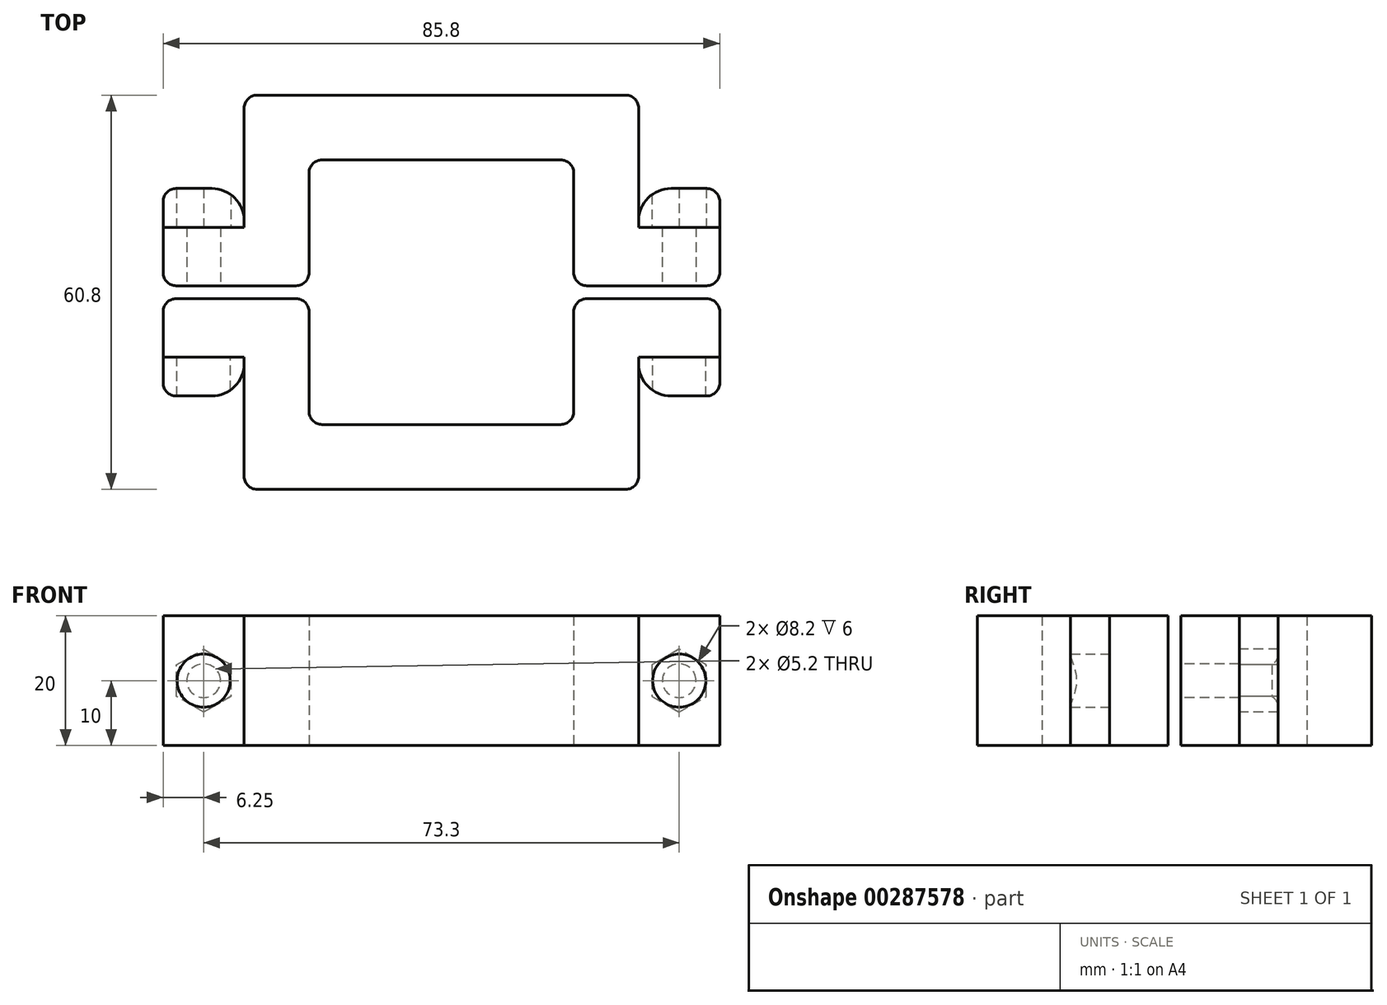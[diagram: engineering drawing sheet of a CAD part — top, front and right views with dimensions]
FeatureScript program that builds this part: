
annotation { "Feature Type Name" : "Feature", "Feature Type Description" : "" }
export const myFeature = defineFeature(function(context is Context, id is Id, definition is map)
    precondition{}
    {
        {
            var Q0;
            Q0=qCreatedBy(makeId("Top.planeOp"),FACE);
            var sketch = newSketch(context, id + "F0", { "sketchPlane" : qUnion([Q0])});
            skLineSegment(sketch, "E0.bottom", {"start": v(20.4, -20.4) * mm, "end": v(-20.4, -20.4) * mm});
            skLineSegment(sketch, "E0.top", {"start": v(20.4, 20.4) * mm, "end": v(-20.4, 20.4) * mm});
            skLineSegment(sketch, "E0.left", {"start": v(20.4, -20.4) * mm, "end": v(20.4, 20.4) * mm});
            skLineSegment(sketch, "E0.right", {"start": v(-20.4, -20.4) * mm, "end": v(-20.4, 20.4) * mm});
            skPoint(sketch, "E0.middle", {"position": v(0, 0) * mm});
            skLineSegment(sketch, "E1.bottom", {"start": v(30.4, -30.4) * mm, "end": v(-30.4, -30.4) * mm});
            skLineSegment(sketch, "E1.top", {"start": v(30.4, 30.4) * mm, "end": v(-30.4, 30.4) * mm});
            skLineSegment(sketch, "E1.left", {"start": v(30.4, -30.4) * mm, "end": v(30.4, 30.4) * mm});
            skLineSegment(sketch, "E1.right", {"start": v(-30.4, -30.4) * mm, "end": v(-30.4, 30.4) * mm});
            skLineSegment(sketch, "E2.bottom", {"start": v(42.9, -10) * mm, "end": v(17.9, -10) * mm});
            skLineSegment(sketch, "E2.top", {"start": v(42.9, 10) * mm, "end": v(17.9, 10) * mm});
            skLineSegment(sketch, "E2.left", {"start": v(42.9, -10) * mm, "end": v(42.9, 10) * mm});
            skLineSegment(sketch, "E2.right", {"start": v(17.9, -10) * mm, "end": v(17.9, 10) * mm});
            skPoint(sketch, "E2.middle", {"position": v(30.4, 0) * mm});
            skLineSegment(sketch, "E3.MirrorCS", {"start": v(-42.9, -10) * mm, "end": v(-17.9, -10) * mm});
            skLineSegment(sketch, "E4.MirrorCS", {"start": v(-42.9, 10) * mm, "end": v(-17.9, 10) * mm});
            skLineSegment(sketch, "E5.MirrorCS", {"start": v(-17.9, -10) * mm, "end": v(-17.9, 10) * mm});
            skLineSegment(sketch, "E6.MirrorCS", {"start": v(-42.9, -10) * mm, "end": v(-42.9, 10) * mm});
            skLineSegment(sketch, "E7.bottom", {"start": v(42.9, 1) * mm, "end": v(-42.9, 1) * mm});
            skLineSegment(sketch, "E7.top", {"start": v(42.9, -1) * mm, "end": v(-42.9, -1) * mm});
            skLineSegment(sketch, "E7.left", {"start": v(42.9, 1) * mm, "end": v(42.9, -1) * mm});
            skLineSegment(sketch, "E7.right", {"start": v(-42.9, 1) * mm, "end": v(-42.9, -1) * mm});
            skSolve(sketch);
        }
        {
            var Q0;
            {var subQ2=sQuery(id+"F0.wireOp",EDGE,"E0.top");Q0=makeQuery(id+"F0.imprint","IMPRINT",FACE,{"disambiguationData":[TD([[makeQuery(id+"F0.imprint","IMPRINT",EDGE,{"derivedFrom":subQ2}),-1.0]])]});}
            var Q1;
            {var subQ0=sQuery(id+"F0.wireOp",EDGE,"E7.bottom");var subQ1=sQuery(id+"F0.wireOp",EDGE,"E0.right");var subQ2=makeQuery(id+"F0.imprint","INTERSECT",VERTEX,{"derivedFrom":[subQ1,subQ0]});Q1=makeQuery(id+"F0.imprint","IMPRINT",FACE,{"disambiguationData":[TD([[makeQuery(id+"F0.imprint","IMPRINT",EDGE,{"disambiguationData":[TD([[subQ2,-1.0]])],"derivedFrom":subQ1}),1.0]])]});}
            var Q2;
            {var subQ0=sQuery(id+"F0.wireOp",EDGE,"E4.MirrorCS");var subQ1=sQuery(id+"F0.wireOp",EDGE,"E1.right");var subQ2=makeQuery(id+"F0.imprint","INTERSECT",VERTEX,{"derivedFrom":[subQ1,subQ0]});Q2=makeQuery(id+"F0.imprint","IMPRINT",FACE,{"disambiguationData":[TD([[makeQuery(id+"F0.imprint","IMPRINT",EDGE,{"disambiguationData":[TD([[subQ2,1.0]])],"derivedFrom":subQ1}),1.0]])]});}
            var Q3;
            {var subQ0=sQuery(id+"F0.wireOp",EDGE,"E3.MirrorCS");var subQ1=sQuery(id+"F0.wireOp",EDGE,"E1.right");var subQ2=makeQuery(id+"F0.imprint","INTERSECT",VERTEX,{"derivedFrom":[subQ1,subQ0]});Q3=makeQuery(id+"F0.imprint","IMPRINT",FACE,{"disambiguationData":[TD([[makeQuery(id+"F0.imprint","IMPRINT",EDGE,{"disambiguationData":[TD([[subQ2,-1.0]])],"derivedFrom":subQ1}),1.0]])]});}
            var Q4;
            {var subQ0=sQuery(id+"F0.wireOp",EDGE,"E3.MirrorCS");var subQ1=sQuery(id+"F0.wireOp",EDGE,"E0.right");var subQ2=makeQuery(id+"F0.imprint","INTERSECT",VERTEX,{"derivedFrom":[subQ1,subQ0]});Q4=makeQuery(id+"F0.imprint","IMPRINT",FACE,{"disambiguationData":[TD([[makeQuery(id+"F0.imprint","IMPRINT",EDGE,{"disambiguationData":[TD([[subQ2,-1.0]])],"derivedFrom":subQ1}),1.0]])]});}
            var Q5;
            {var subQ2=sQuery(id+"F0.wireOp",EDGE,"E0.bottom");Q5=makeQuery(id+"F0.imprint","IMPRINT",FACE,{"disambiguationData":[TD([[makeQuery(id+"F0.imprint","IMPRINT",EDGE,{"derivedFrom":subQ2}),1.0]])]});}
            var Q6;
            {var subQ0=sQuery(id+"F0.wireOp",EDGE,"E2.bottom");var subQ1=sQuery(id+"F0.wireOp",EDGE,"E1.left");var subQ2=makeQuery(id+"F0.imprint","INTERSECT",VERTEX,{"derivedFrom":[subQ1,subQ0]});Q6=makeQuery(id+"F0.imprint","IMPRINT",FACE,{"disambiguationData":[TD([[makeQuery(id+"F0.imprint","IMPRINT",EDGE,{"disambiguationData":[TD([[subQ2,-1.0]])],"derivedFrom":subQ1}),-1.0]])]});}
            var Q7;
            {var subQ0=sQuery(id+"F0.wireOp",EDGE,"E2.bottom");var subQ1=sQuery(id+"F0.wireOp",EDGE,"E0.left");var subQ2=makeQuery(id+"F0.imprint","INTERSECT",VERTEX,{"derivedFrom":[subQ1,subQ0]});Q7=makeQuery(id+"F0.imprint","IMPRINT",FACE,{"disambiguationData":[TD([[makeQuery(id+"F0.imprint","IMPRINT",EDGE,{"disambiguationData":[TD([[subQ2,-1.0]])],"derivedFrom":subQ1}),-1.0]])]});}
            var Q8;
            {var subQ0=sQuery(id+"F0.wireOp",EDGE,"E2.top");var subQ1=sQuery(id+"F0.wireOp",EDGE,"E1.left");var subQ2=makeQuery(id+"F0.imprint","INTERSECT",VERTEX,{"derivedFrom":[subQ1,subQ0]});Q8=makeQuery(id+"F0.imprint","IMPRINT",FACE,{"disambiguationData":[TD([[makeQuery(id+"F0.imprint","IMPRINT",EDGE,{"disambiguationData":[TD([[subQ2,1.0]])],"derivedFrom":subQ1}),-1.0]])]});}
            var Q9;
            {var subQ0=sQuery(id+"F0.wireOp",EDGE,"E2.top");var subQ1=sQuery(id+"F0.wireOp",EDGE,"E0.left");var subQ2=makeQuery(id+"F0.imprint","INTERSECT",VERTEX,{"derivedFrom":[subQ1,subQ0]});Q9=makeQuery(id+"F0.imprint","IMPRINT",FACE,{"disambiguationData":[TD([[makeQuery(id+"F0.imprint","IMPRINT",EDGE,{"disambiguationData":[TD([[subQ2,1.0]])],"derivedFrom":subQ1}),-1.0]])]});}
            extrude(context, id + "F1", {"entities" : qUnion([Q0, Q1, Q2, Q3, Q4, Q5, Q6, Q7, Q8, Q9]), "depth" : 20 * mm, "offsetDistance" : 25 * mm});
        }
        {
            var Q0;
            Q0=makeQuery(id+"F1.opExtrude","SWEPT_FACE",FACE,{"disambiguationData":[OSD([sQuery(id+"F0.wireOp",EDGE,"E2.bottom")])]});
            var sketch = newSketch(context, id + "F2", { "sketchPlane" : qUnion([Q0])});
            skCircle(sketch, "E8", {"center": v(36.65, 10) * mm, "radius": 2.6 * mm});
            skPoint(sketch, "E8.centerSnap0", {"position": v(36.65, 20) * mm});
            skPoint(sketch, "E8.centerSnap1", {"position": v(42.9, 10) * mm});
            skCircle(sketch, "E9", {"center": v(36.65, 10) * mm, "radius": 4.1 * mm});
            skSolve(sketch);
        }
        {
            var Q0;
            Q0=makeQuery(id+"F2.imprint","IMPRINT",FACE,{"disambiguationData":[TD([[makeQuery(id+"F2.imprint","IMPRINT",EDGE,{"derivedFrom":sQuery(id+"F2.wireOp",EDGE,"E8")}),1.0]])]});
            var Q1;
            Q1=makeQuery(id+"F1.opExtrude","SWEPT_FACE",FACE,{"disambiguationData":[OSD([sQuery(id+"F0.wireOp",EDGE,"E2.top")])]});
            extrude(context, id + "F3", {"entities" : qUnion([Q0]), "endBound" : BoundingType.UP_TO_SURFACE, "oppositeDirection" : true, "depth" : 25 * mm, "endBoundEntityFace" : qUnion([Q1]), "offsetDistance" : 25 * mm});
        }
        {
            var Q0;
            Q0=makeQuery(id+"F2.imprint","IMPRINT",FACE,{"disambiguationData":[TD([[makeQuery(id+"F2.imprint","IMPRINT",EDGE,{"derivedFrom":sQuery(id+"F2.wireOp",EDGE,"E9")}),-1.0]])]});
            extrude(context, id + "F4", {"entities" : qUnion([Q0]), "depth" : 6 * mm, "offsetDistance" : 25 * mm});
        }
        {
            var Q0;
            Q0=makeQuery(id+"F1.opExtrude","SWEPT_FACE",FACE,{"disambiguationData":[OSD([sQuery(id+"F0.wireOp",EDGE,"E2.top")])]});
            var sketch = newSketch(context, id + "F5", { "sketchPlane" : qUnion([Q0])});
            skCircle(sketch, "E10.cCircle", {"center": v(-36.65, 10) * mm, "radius": 4.2 * mm, "construction": true});
            skPoint(sketch, "E10.cCircle.centerSnap0", {"position": v(-42.9, 10) * mm});
            skPoint(sketch, "E10.cCircle.centerSnap1", {"position": v(-36.65, 20) * mm});
            skLineSegment(sketch, "E10.0", {"start": v(-32.45, 7.58) * mm, "end": v(-36.65, 5.15) * mm});
            skLineSegment(sketch, "E10.1", {"start": v(-36.65, 5.15) * mm, "end": v(-40.85, 7.58) * mm});
            skLineSegment(sketch, "E10.2", {"start": v(-40.85, 7.58) * mm, "end": v(-40.85, 12.42) * mm});
            skLineSegment(sketch, "E10.3", {"start": v(-40.85, 12.42) * mm, "end": v(-36.65, 14.85) * mm});
            skLineSegment(sketch, "E10.4", {"start": v(-36.65, 14.85) * mm, "end": v(-32.45, 12.42) * mm});
            skLineSegment(sketch, "E10.5", {"start": v(-32.45, 12.42) * mm, "end": v(-32.45, 7.58) * mm});
            skPoint(sketch, "E10.0.midPoint", {"position": v(-34.55, 6.36) * mm});
            skSolve(sketch);
        }
        {
            var Q0;
            Q0=makeQuery(id+"F5.imprint","IMPRINT",FACE,{"disambiguationData":[TD([[makeQuery(id+"F5.imprint","IMPRINT",EDGE,{"derivedFrom":sQuery(id+"F5.wireOp",EDGE,"E10.0")}),1.0]])]});
            extrude(context, id + "F6", {"entities" : qUnion([Q0]), "depth" : 6 * mm, "offsetDistance" : 25 * mm});
        }
        {
            var Q0;
            Q0=makeQuery(id+"F4.opExtrude","SWEPT_BODY",BODY,{"disambiguationData":[OSD([sQuery(id+"F0.wireOp",EDGE,"E1.left"),sQuery(id+"F0.wireOp",EDGE,"E2.bottom"),sQuery(id+"F0.wireOp",EDGE,"E2.left"),sQuery(id+"F2.wireOp",EDGE,"E9")])]});
            var Q1;
            Q1=makeQuery(id+"F3.opExtrude","SWEPT_BODY",BODY,{"disambiguationData":[OSD([sQuery(id+"F2.wireOp",EDGE,"E8")])]});
            var Q2;
            Q2=makeQuery(id+"F6.opExtrude","SWEPT_BODY",BODY,{"disambiguationData":[OSD([sQuery(id+"F0.wireOp",EDGE,"E1.left"),sQuery(id+"F0.wireOp",EDGE,"E2.top"),sQuery(id+"F0.wireOp",EDGE,"E2.left"),sQuery(id+"F5.wireOp",EDGE,"E10.0"),sQuery(id+"F5.wireOp",EDGE,"E10.1"),sQuery(id+"F5.wireOp",EDGE,"E10.2"),sQuery(id+"F5.wireOp",EDGE,"E10.3"),sQuery(id+"F5.wireOp",EDGE,"E10.4"),sQuery(id+"F5.wireOp",EDGE,"E10.5")])]});
            var Q3;
            Q3=qCreatedBy(makeId("Right.planeOp"),FACE);
            mirror(context, id + "F7", {"entities" : qUnion([Q0, Q1, Q2]), "mirrorPlane" : qUnion([Q3])});
        }
        {
            var Q0;
            Q0=makeQuery(id+"F7.opPattern","COPY",BODY,{"derivedFrom":makeQuery(id+"F3.opExtrude","SWEPT_BODY",BODY,{"disambiguationData":[OSD([sQuery(id+"F2.wireOp",EDGE,"E8")])]}),"instanceName":"1"});
            var Q1;
            Q1=makeQuery(id+"F3.opExtrude","SWEPT_BODY",BODY,{"disambiguationData":[OSD([sQuery(id+"F2.wireOp",EDGE,"E8")])]});
            var Q2;
            Q2=makeQuery(id+"F4.opExtrude","SWEPT_BODY",BODY,{"disambiguationData":[OSD([sQuery(id+"F0.wireOp",EDGE,"E1.left"),sQuery(id+"F0.wireOp",EDGE,"E2.bottom"),sQuery(id+"F0.wireOp",EDGE,"E2.left"),sQuery(id+"F2.wireOp",EDGE,"E9")])]});
            var Q3;
            Q3=makeQuery(id+"F1.opExtrude","SWEPT_BODY",BODY,{"disambiguationData":[OSD([sQuery(id+"F0.wireOp",EDGE,"E0.top"),sQuery(id+"F0.wireOp",EDGE,"E0.left"),sQuery(id+"F0.wireOp",EDGE,"E0.right"),sQuery(id+"F0.wireOp",EDGE,"E1.top"),sQuery(id+"F0.wireOp",EDGE,"E1.left"),sQuery(id+"F0.wireOp",EDGE,"E1.right"),sQuery(id+"F0.wireOp",EDGE,"E2.top"),sQuery(id+"F0.wireOp",EDGE,"E2.left"),sQuery(id+"F0.wireOp",EDGE,"E4.MirrorCS"),sQuery(id+"F0.wireOp",EDGE,"E6.MirrorCS"),sQuery(id+"F0.wireOp",EDGE,"E7.bottom")])]});
            booleanBodies(context, id + "F8", {"operationType" : BooleanOperationType.SUBTRACTION, "tools" : qUnion([Q0, Q1]), "targets" : qUnion([Q2, Q3])});
        }
        {
            var Q0;
            Q0=makeQuery(id+"F1.opExtrude","SWEPT_EDGE",EDGE,{"disambiguationData":[OSD([sQuery(id+"F0.wireOp",EDGE,"E0.top"),sQuery(id+"F0.wireOp",EDGE,"E0.right")])]});
            var Q1;
            Q1=makeQuery(id+"F1.opExtrude","SWEPT_EDGE",EDGE,{"disambiguationData":[OSD([sQuery(id+"F0.wireOp",EDGE,"E0.top"),sQuery(id+"F0.wireOp",EDGE,"E0.left")])]});
            var Q2;
            Q2=makeQuery(id+"F1.opExtrude","SWEPT_EDGE",EDGE,{"disambiguationData":[OSD([sQuery(id+"F0.wireOp",EDGE,"E0.bottom"),sQuery(id+"F0.wireOp",EDGE,"E0.left")])]});
            var Q3;
            Q3=makeQuery(id+"F1.opExtrude","SWEPT_EDGE",EDGE,{"disambiguationData":[OSD([sQuery(id+"F0.wireOp",EDGE,"E0.bottom"),sQuery(id+"F0.wireOp",EDGE,"E0.right")])]});
            fillet(context, id + "F9", {"entities" : qUnion([Q0, Q1, Q2, Q3]), "tangentPropagation" : true, "radius" : 2 * mm, "defaultsChanged" : true, "vertexSettings" : [], "allowEdgeOverflow" : false});
        }
        {
            var Q0;
            Q0=makeQuery(id+"F1.opExtrude","SWEPT_EDGE",EDGE,{"disambiguationData":[OSD([sQuery(id+"F0.wireOp",EDGE,"E0.right"),sQuery(id+"F0.wireOp",EDGE,"E7.bottom")])]});
            var Q1;
            Q1=makeQuery(id+"F1.opExtrude","SWEPT_EDGE",EDGE,{"disambiguationData":[OSD([sQuery(id+"F0.wireOp",EDGE,"E0.right"),sQuery(id+"F0.wireOp",EDGE,"E7.top")])]});
            var Q2;
            Q2=makeQuery(id+"F1.opExtrude","SWEPT_EDGE",EDGE,{"disambiguationData":[OSD([sQuery(id+"F0.wireOp",EDGE,"E0.left"),sQuery(id+"F0.wireOp",EDGE,"E7.top")])]});
            var Q3;
            Q3=makeQuery(id+"F1.opExtrude","SWEPT_EDGE",EDGE,{"disambiguationData":[OSD([sQuery(id+"F0.wireOp",EDGE,"E0.left"),sQuery(id+"F0.wireOp",EDGE,"E7.bottom")])]});
            var Q4;
            Q4=makeQuery(id+"F1.opExtrude","SWEPT_EDGE",EDGE,{"disambiguationData":[OSD([sQuery(id+"F0.wireOp",EDGE,"E2.left"),sQuery(id+"F0.wireOp",EDGE,"E7.top")])]});
            var Q5;
            Q5=makeQuery(id+"F6.opExtrude","CAP_EDGE",EDGE,{"disambiguationData":[OSD([sQuery(id+"F0.wireOp",EDGE,"E2.top"),sQuery(id+"F0.wireOp",EDGE,"E2.left")])],"isStart":false});
            var Q6;
            Q6=makeQuery(id+"F4.opExtrude","CAP_EDGE",EDGE,{"disambiguationData":[OSD([sQuery(id+"F0.wireOp",EDGE,"E2.bottom"),sQuery(id+"F0.wireOp",EDGE,"E2.left")])],"isStart":false});
            var Q7;
            Q7=makeQuery(id+"F1.opExtrude","SWEPT_EDGE",EDGE,{"disambiguationData":[OSD([sQuery(id+"F0.wireOp",EDGE,"E2.left"),sQuery(id+"F0.wireOp",EDGE,"E7.bottom")])]});
            var Q8;
            Q8=makeQuery(id+"F7.opPattern","COPY",EDGE,{"derivedFrom":makeQuery(id+"F4.opExtrude","CAP_EDGE",EDGE,{"disambiguationData":[OSD([sQuery(id+"F0.wireOp",EDGE,"E2.bottom"),sQuery(id+"F0.wireOp",EDGE,"E2.left")])],"isStart":false}),"instanceName":"1"});
            var Q9;
            Q9=makeQuery(id+"F1.opExtrude","SWEPT_EDGE",EDGE,{"disambiguationData":[OSD([sQuery(id+"F0.wireOp",EDGE,"E6.MirrorCS"),sQuery(id+"F0.wireOp",EDGE,"E7.top")])]});
            var Q10;
            Q10=makeQuery(id+"F1.opExtrude","SWEPT_EDGE",EDGE,{"disambiguationData":[OSD([sQuery(id+"F0.wireOp",EDGE,"E6.MirrorCS"),sQuery(id+"F0.wireOp",EDGE,"E7.bottom")])]});
            var Q11;
            Q11=makeQuery(id+"F7.opPattern","COPY",EDGE,{"derivedFrom":makeQuery(id+"F6.opExtrude","CAP_EDGE",EDGE,{"disambiguationData":[OSD([sQuery(id+"F0.wireOp",EDGE,"E2.top"),sQuery(id+"F0.wireOp",EDGE,"E2.left")])],"isStart":false}),"instanceName":"1"});
            var Q12;
            Q12=makeQuery(id+"F1.opExtrude","SWEPT_EDGE",EDGE,{"disambiguationData":[OSD([sQuery(id+"F0.wireOp",EDGE,"E1.bottom"),sQuery(id+"F0.wireOp",EDGE,"E1.left")])]});
            var Q13;
            Q13=makeQuery(id+"F1.opExtrude","SWEPT_EDGE",EDGE,{"disambiguationData":[OSD([sQuery(id+"F0.wireOp",EDGE,"E1.bottom"),sQuery(id+"F0.wireOp",EDGE,"E1.right")])]});
            var Q14;
            Q14=makeQuery(id+"F1.opExtrude","SWEPT_EDGE",EDGE,{"disambiguationData":[OSD([sQuery(id+"F0.wireOp",EDGE,"E1.top"),sQuery(id+"F0.wireOp",EDGE,"E1.left")])]});
            var Q15;
            Q15=makeQuery(id+"F1.opExtrude","SWEPT_EDGE",EDGE,{"disambiguationData":[OSD([sQuery(id+"F0.wireOp",EDGE,"E1.top"),sQuery(id+"F0.wireOp",EDGE,"E1.right")])]});
            fillet(context, id + "F10", {"entities" : qUnion([Q0, Q1, Q2, Q3, Q4, Q5, Q6, Q7, Q8, Q9, Q10, Q11, Q12, Q13, Q14, Q15]), "tangentPropagation" : true, "radius" : 2 * mm, "defaultsChanged" : false, "vertexSettings" : [], "allowEdgeOverflow" : false});
        }
        {
            var Q0;
            Q0=makeQuery(id+"F4.opExtrude","CAP_EDGE",EDGE,{"disambiguationData":[OSD([sQuery(id+"F0.wireOp",EDGE,"E1.left"),sQuery(id+"F0.wireOp",EDGE,"E2.bottom")])],"isStart":false});
            var Q1;
            Q1=makeQuery(id+"F7.opPattern","COPY",EDGE,{"derivedFrom":makeQuery(id+"F4.opExtrude","CAP_EDGE",EDGE,{"disambiguationData":[OSD([sQuery(id+"F0.wireOp",EDGE,"E1.left"),sQuery(id+"F0.wireOp",EDGE,"E2.bottom")])],"isStart":false}),"instanceName":"1"});
            var Q2;
            Q2=makeQuery(id+"F7.opPattern","COPY",EDGE,{"derivedFrom":makeQuery(id+"F6.opExtrude","CAP_EDGE",EDGE,{"disambiguationData":[OSD([sQuery(id+"F0.wireOp",EDGE,"E1.left"),sQuery(id+"F0.wireOp",EDGE,"E2.top")])],"isStart":false}),"instanceName":"1"});
            var Q3;
            Q3=makeQuery(id+"F6.opExtrude","CAP_EDGE",EDGE,{"disambiguationData":[OSD([sQuery(id+"F0.wireOp",EDGE,"E1.left"),sQuery(id+"F0.wireOp",EDGE,"E2.top")])],"isStart":false});
            fillet(context, id + "F11", {"entities" : qUnion([Q0, Q1, Q2, Q3]), "tangentPropagation" : true, "radius" : 5 * mm, "defaultsChanged" : false, "vertexSettings" : [], "allowEdgeOverflow" : false});
        }
    });
